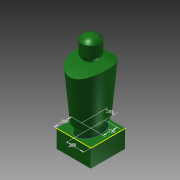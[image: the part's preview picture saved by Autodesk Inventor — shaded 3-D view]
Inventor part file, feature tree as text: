
AUTODESK INVENTOR PART (.ipt)
format: ipt  version: 2015 (Build 190159000, 159)  size: 193,024 bytes
history: native  units: in
note: dims shown in document units (in); Inventor stores cm internally (conversion verified against a paired STEP export)
features: sketch x5, extrude x4, projected_geometry x2, plane x1, revolve x1
ambient origin geometry x8: Origin, YZ Plane, XZ Plane, XY Plane, X Axis, Y Axis, Z Axis, Center Point
bodies: Solid1 (feature_tree)
feature tree (13):
  extrude  "Extrusion1"  Depth=0.575in
  sketch  "Sketch2"  dims[d2=0.3in d3=0.0in d4=0.2875in]
  extrude  "Extrusion2"  Depth=0.2875in
  extrude  "Extrusion3"  Depth=0.236in
  plane  "Work Plane2"
  extrude  "Extrusion4"  Depth=0.155in TaperAngle=0.0deg
  revolve  "Revolution1"  [1 undecoded]
  sketch  "Sketch1"  dims[d0=0.575in d1=0.575in]
  sketch  "Sketch3"  dims[d5=0.2875in d6=0.236in]
  sketch  "Sketch4"  dims[d7=0.155in d8=0.155in d9=0.0in]
  sketch  "Sketch5"  dims[d10=0.2875in d11=0.2875in d12=0.286in d13=0.205in d14=0.84in d15=0.0344in d16=1.2in d17=0.6in d18=1.05in d19=1.0in d20=0.0in d21=90.0deg d22=0.3801in d23=0.0709in d24=0.119in]
  projected_geometry  "Projected Loop1"
  projected_geometry  "Projected Loop2"
note: 1 required parameter value undecoded (feature->parameter linkage not recoverable at this tier; creation-order binding heuristic only, values carry confidence <= 0.55)
